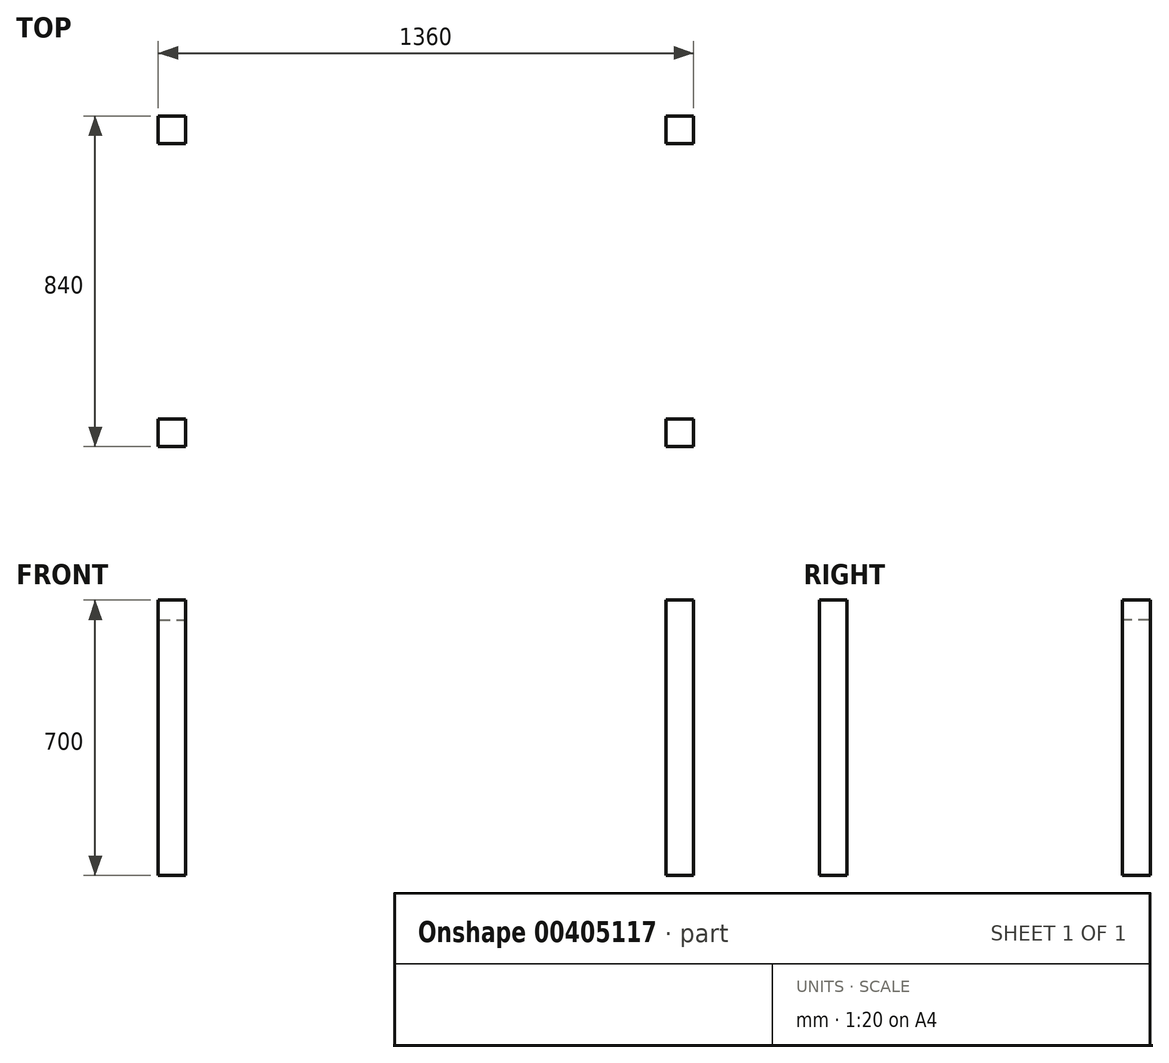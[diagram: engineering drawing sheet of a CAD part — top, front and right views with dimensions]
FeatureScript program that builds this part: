
annotation { "Feature Type Name" : "Feature", "Feature Type Description" : "" }
export const myFeature = defineFeature(function(context is Context, id is Id, definition is map)
    precondition{}
    {
        {
            var Q0;
            Q0=qCreatedBy(makeId("Top.planeOp"),FACE);
            var sketch = newSketch(context, id + "F0", { "sketchPlane" : qUnion([Q0])});
            skLineSegment(sketch, "E0.bottom", {"start": v(-680, 420) * mm, "end": v(680, 420) * mm});
            skLineSegment(sketch, "E0.top", {"start": v(-680, -420) * mm, "end": v(680, -420) * mm});
            skLineSegment(sketch, "E0.left", {"start": v(-680, 420) * mm, "end": v(-680, -420) * mm});
            skLineSegment(sketch, "E0.right", {"start": v(680, 420) * mm, "end": v(680, -420) * mm});
            skLineSegment(sketch, "E1.bottom", {"start": v(-680, 420) * mm, "end": v(-610, 420) * mm});
            skLineSegment(sketch, "E1.top", {"start": v(-680, 350) * mm, "end": v(-610, 350) * mm});
            skLineSegment(sketch, "E1.left", {"start": v(-680, 420) * mm, "end": v(-680, 350) * mm});
            skLineSegment(sketch, "E1.right", {"start": v(-610, 420) * mm, "end": v(-610, 350) * mm});
            skLineSegment(sketch, "E2.bottom", {"start": v(-610, 350) * mm, "end": v(610, 350) * mm, "construction": true});
            skLineSegment(sketch, "E2.top", {"start": v(-610, -350) * mm, "end": v(610, -350) * mm, "construction": true});
            skLineSegment(sketch, "E2.left", {"start": v(-610, 350) * mm, "end": v(-610, -350) * mm, "construction": true});
            skLineSegment(sketch, "E2.right", {"start": v(610, 350) * mm, "end": v(610, -350) * mm, "construction": true});
            skLineSegment(sketch, "E3.bottom", {"start": v(-610, -350) * mm, "end": v(-680, -350) * mm});
            skLineSegment(sketch, "E3.top", {"start": v(-610, -420) * mm, "end": v(-680, -420) * mm});
            skLineSegment(sketch, "E3.left", {"start": v(-610, -350) * mm, "end": v(-610, -420) * mm});
            skLineSegment(sketch, "E3.right", {"start": v(-680, -350) * mm, "end": v(-680, -420) * mm});
            skLineSegment(sketch, "E4.bottom", {"start": v(610, -350) * mm, "end": v(680, -350) * mm});
            skLineSegment(sketch, "E4.top", {"start": v(610, -420) * mm, "end": v(680, -420) * mm});
            skLineSegment(sketch, "E4.left", {"start": v(610, -350) * mm, "end": v(610, -420) * mm});
            skLineSegment(sketch, "E4.right", {"start": v(680, -350) * mm, "end": v(680, -420) * mm});
            skLineSegment(sketch, "E5.bottom", {"start": v(610, 350) * mm, "end": v(680, 350) * mm});
            skLineSegment(sketch, "E5.top", {"start": v(610, 420) * mm, "end": v(680, 420) * mm});
            skLineSegment(sketch, "E5.left", {"start": v(610, 350) * mm, "end": v(610, 420) * mm});
            skLineSegment(sketch, "E5.right", {"start": v(680, 350) * mm, "end": v(680, 420) * mm});
            skSolve(sketch);
        }
        {
            var Q0;
            Q0=makeQuery(id+"F0.imprint","IMPRINT",FACE,{"disambiguationData":[TD([[makeQuery(id+"F0.imprint","IMPRINT",EDGE,{"derivedFrom":sQuery(id+"F0.wireOp",EDGE,"E1.bottom")}),-1.0]])]});
            var Q1;
            Q1=makeQuery(id+"F0.imprint","IMPRINT",FACE,{"disambiguationData":[TD([[makeQuery(id+"F0.imprint","IMPRINT",EDGE,{"derivedFrom":sQuery(id+"F0.wireOp",EDGE,"E5.bottom")}),1.0]])]});
            var Q2;
            Q2=makeQuery(id+"F0.imprint","IMPRINT",FACE,{"disambiguationData":[TD([[makeQuery(id+"F0.imprint","IMPRINT",EDGE,{"derivedFrom":sQuery(id+"F0.wireOp",EDGE,"E4.bottom")}),-1.0]])]});
            var Q3;
            Q3=makeQuery(id+"F0.imprint","IMPRINT",FACE,{"disambiguationData":[TD([[makeQuery(id+"F0.imprint","IMPRINT",EDGE,{"derivedFrom":sQuery(id+"F0.wireOp",EDGE,"E3.bottom")}),1.0]])]});
            extrude(context, id + "F1", {"entities" : qUnion([Q0, Q1, Q2, Q3]), "depth" : 650 * mm});
        }
        {
            var Q0;
            Q0=makeQuery(id+"F0.imprint","IMPRINT",FACE,{"disambiguationData":[TD([[makeQuery(id+"F0.imprint","IMPRINT",EDGE,{"derivedFrom":sQuery(id+"F0.wireOp",EDGE,"E1.bottom")}),-1.0]])]});
            var Q1;
            Q1=makeQuery(id+"F0.imprint","IMPRINT",FACE,{"disambiguationData":[TD([[makeQuery(id+"F0.imprint","IMPRINT",EDGE,{"derivedFrom":sQuery(id+"F0.wireOp",EDGE,"E0.bottom")}),-1.0]])]});
            var Q2;
            Q2=makeQuery(id+"F0.imprint","IMPRINT",FACE,{"disambiguationData":[TD([[makeQuery(id+"F0.imprint","IMPRINT",EDGE,{"derivedFrom":sQuery(id+"F0.wireOp",EDGE,"E3.bottom")}),1.0]])]});
            var Q3;
            Q3=makeQuery(id+"F0.imprint","IMPRINT",FACE,{"disambiguationData":[TD([[makeQuery(id+"F0.imprint","IMPRINT",EDGE,{"derivedFrom":sQuery(id+"F0.wireOp",EDGE,"E5.bottom")}),1.0]])]});
            var Q4;
            Q4=makeQuery(id+"F0.imprint","IMPRINT",FACE,{"disambiguationData":[TD([[makeQuery(id+"F0.imprint","IMPRINT",EDGE,{"derivedFrom":sQuery(id+"F0.wireOp",EDGE,"E4.bottom")}),-1.0]])]});
            extrude(context, id + "F2", {"entities" : qUnion([Q0, Q1, Q2, Q3, Q4]), "operationType" : NewBodyOperationType.ADD, "depth" : 700 * mm, "hasSecondDirection" : true, "secondDirectionOppositeDirection" : false, "secondDirectionDepth" : 650 * mm});
        }
    });
